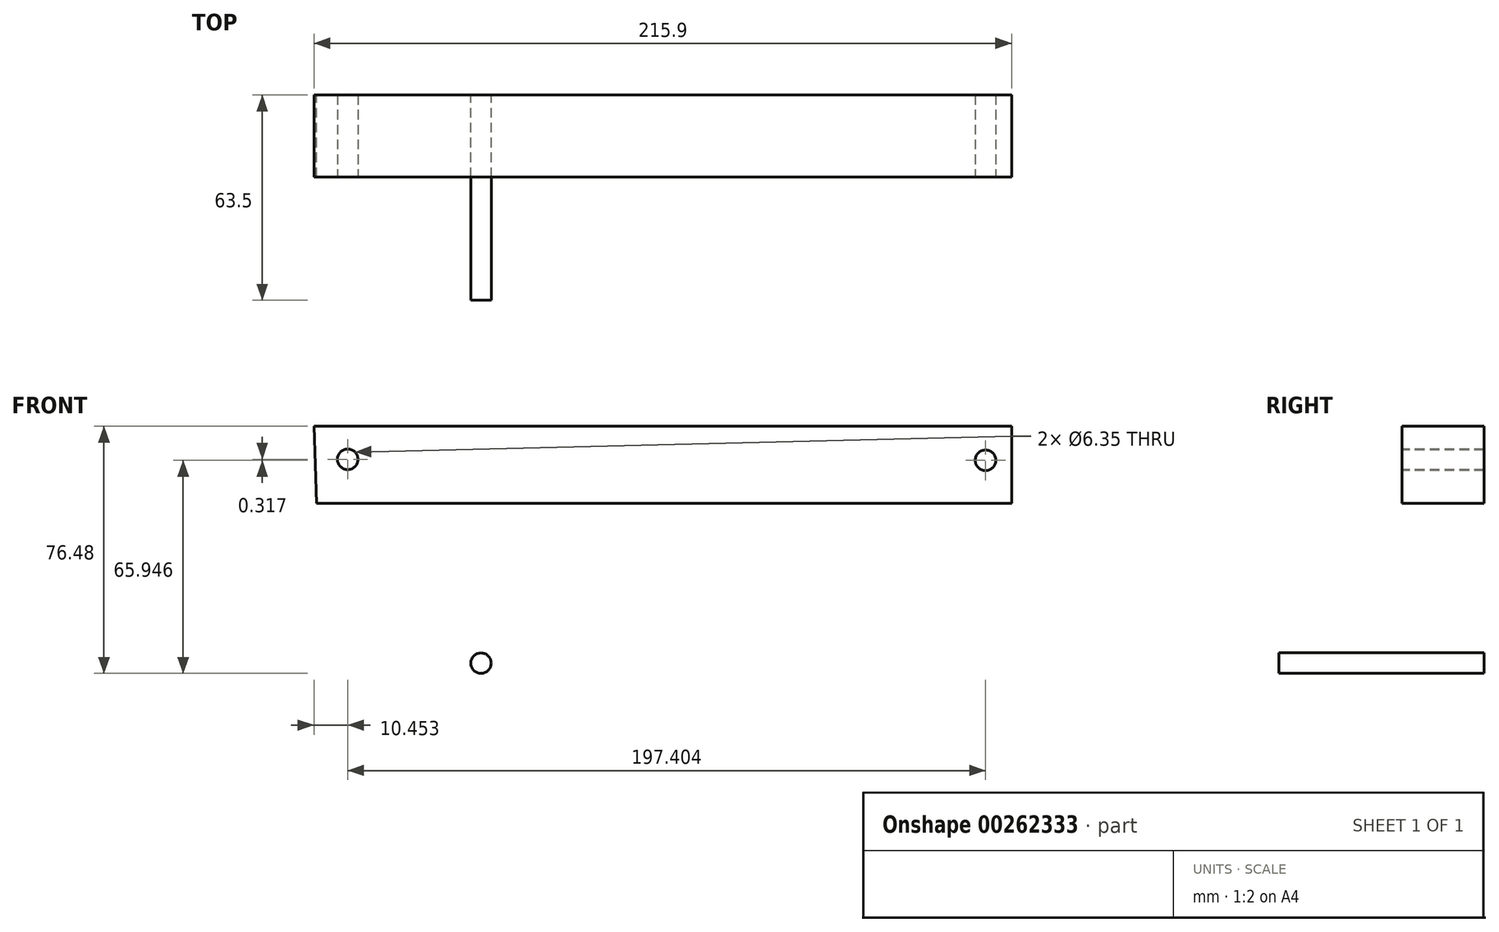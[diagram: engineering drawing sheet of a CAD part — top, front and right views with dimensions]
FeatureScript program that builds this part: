
annotation { "Feature Type Name" : "Feature", "Feature Type Description" : "" }
export const myFeature = defineFeature(function(context is Context, id is Id, definition is map)
    precondition{}
    {
        {
            var Q0;
            Q0=qCreatedBy(makeId("Front.planeOp"),FACE);
            var sketch = newSketch(context, id + "F0", { "sketchPlane" : qUnion([Q0])});
            skLineSegment(sketch, "E0", {"start": v(-83.57, 43.8) * mm, "end": v(132.33, 43.8) * mm});
            skLineSegment(sketch, "E1", {"start": v(132.33, 43.8) * mm, "end": v(132.33, 19.98) * mm});
            skLineSegment(sketch, "E2", {"start": v(132.33, 19.98) * mm, "end": v(-82.8, 19.98) * mm});
            skLineSegment(sketch, "E3", {"start": v(-82.8, 19.98) * mm, "end": v(-83.57, 43.8) * mm});
            skSolve(sketch);
        }
        {
            var Q0;
            Q0=makeQuery(id+"F0.imprint","IMPRINT",FACE,{"disambiguationData":[TD([[makeQuery(id+"F0.imprint","IMPRINT",EDGE,{"derivedFrom":sQuery(id+"F0.wireOp",EDGE,"E0")}),-1.0]])]});
            extrude(context, id + "F1", {"entities" : qUnion([Q0]), "depth" : 25.4 * mm});
        }
        {
            var Q0;
            Q0=makeQuery(id+"F1.opExtrude","CAP_FACE",FACE,{"disambiguationData":[OSD([sQuery(id+"F0.wireOp",EDGE,"E0"),sQuery(id+"F0.wireOp",EDGE,"E1"),sQuery(id+"F0.wireOp",EDGE,"E2"),sQuery(id+"F0.wireOp",EDGE,"E3")])],"isStart":false});
            var sketch = newSketch(context, id + "F2", { "sketchPlane" : qUnion([Q0])});
            skCircle(sketch, "E4", {"center": v(-73.12, 33.58) * mm, "radius": 3.18 * mm});
            skLineSegment(sketch, "E5", {"start": v(132.33, 19.98) * mm, "end": v(56.13, 19.98) * mm});
            skLineSegment(sketch, "E6", {"start": v(56.13, 19.98) * mm, "end": v(56.13, 31.1) * mm});
            skLineSegment(sketch, "E7", {"start": v(56.13, 31.1) * mm, "end": v(56.13, 43.8) * mm});
            skLineSegment(sketch, "E8", {"start": v(56.13, 43.8) * mm, "end": v(56.13, 31.1) * mm});
            skLineSegment(sketch, "E9", {"start": v(43.43, 31.1) * mm, "end": v(56.13, 31.1) * mm});
            skLineSegment(sketch, "E10", {"start": v(43.43, 31.1) * mm, "end": v(37.08, 43.8) * mm});
            skLineSegment(sketch, "E11", {"start": v(56.13, 43.8) * mm, "end": v(37.08, 43.8) * mm});
            skCircle(sketch, "E12", {"center": v(124.29, 33.27) * mm, "radius": 3.18 * mm});
            skSolve(sketch);
        }
        {
            var Q0;
            Q0=makeQuery(id+"F2.imprint","IMPRINT",FACE,{"disambiguationData":[TD([[makeQuery(id+"F2.imprint","IMPRINT",EDGE,{"derivedFrom":sQuery(id+"F2.wireOp",EDGE,"E4")}),1.0]])]});
            var Q1;
            Q1=makeQuery(id+"F2.imprint","IMPRINT",FACE,{"disambiguationData":[TD([[makeQuery(id+"F2.imprint","IMPRINT",EDGE,{"derivedFrom":sQuery(id+"F2.wireOp",EDGE,"fV7eC2Kh-GHSl-BDtu-HwB4-ym4KzGdfG4S1")}),1.0]])]});
            var Q2;
            Q2=makeQuery(id+"F2.imprint","IMPRINT",FACE,{"disambiguationData":[TD([[makeQuery(id+"F2.imprint","IMPRINT",EDGE,{"derivedFrom":sQuery(id+"F2.wireOp",EDGE,"E8")}),-1.0]])]});
            var Q3;
            Q3=makeQuery(id+"F2.imprint","IMPRINT",FACE,{"disambiguationData":[TD([[makeQuery(id+"F2.imprint","IMPRINT",EDGE,{"derivedFrom":sQuery(id+"F2.wireOp",EDGE,"E12")}),1.0]])]});
            extrude(context, id + "F3", {"entities" : qUnion([Q0, Q1, Q2, Q3]), "operationType" : NewBodyOperationType.REMOVE, "endBound" : BoundingType.THROUGH_ALL, "oppositeDirection" : true, "depth" : 25.4 * mm});
        }
        {
            var Q0;
            Q0=qCreatedBy(makeId("Front.planeOp"),FACE);
            var sketch = newSketch(context, id + "F4", { "sketchPlane" : qUnion([Q0])});
            skCircle(sketch, "E13", {"center": v(-31.87, -29.5) * mm, "radius": 3.18 * mm});
            skSolve(sketch);
        }
        {
            var Q0;
            Q0=makeQuery(id+"F4.imprint","IMPRINT",FACE,{"disambiguationData":[TD([[makeQuery(id+"F4.imprint","IMPRINT",EDGE,{"derivedFrom":sQuery(id+"F4.wireOp",EDGE,"E13")}),1.0]])]});
            extrude(context, id + "F5", {"entities" : qUnion([Q0]), "depth" : 63.5 * mm});
        }
    });
